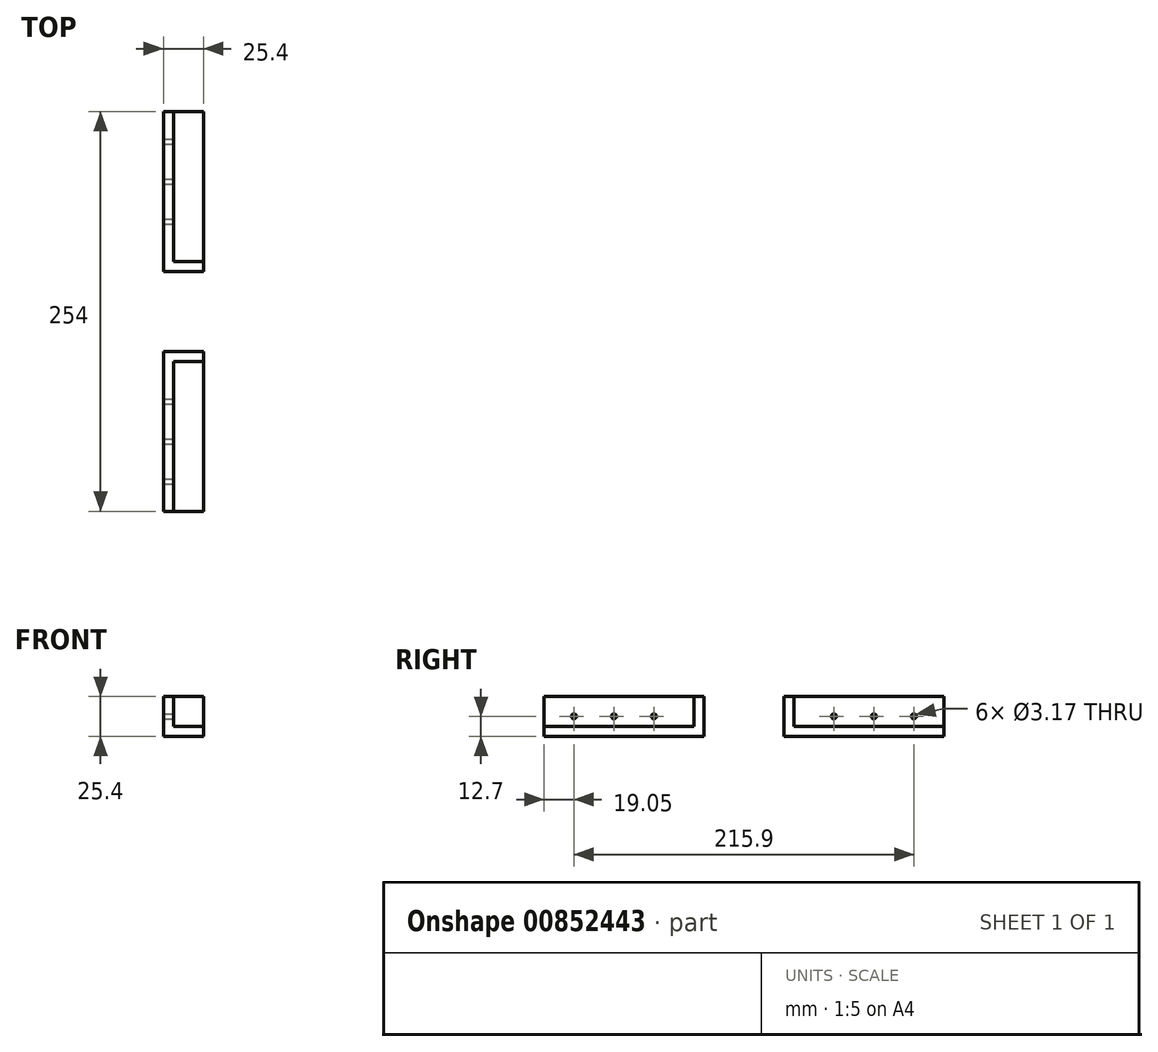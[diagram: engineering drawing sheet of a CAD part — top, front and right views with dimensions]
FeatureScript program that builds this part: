
annotation { "Feature Type Name" : "Feature", "Feature Type Description" : "" }
export const myFeature = defineFeature(function(context is Context, id is Id, definition is map)
    precondition{}
    {
        {
            var Q0;
            Q0=qCreatedBy(makeId("Front.planeOp"),FACE);
            var sketch = newSketch(context, id + "F0", { "sketchPlane" : qUnion([Q0])});
            skLineSegment(sketch, "E0", {"start": v(0, 0) * mm, "end": v(0, 25.4) * mm});
            skLineSegment(sketch, "E1", {"start": v(0, 25.4) * mm, "end": v(6.35, 25.4) * mm});
            skLineSegment(sketch, "E2", {"start": v(6.35, 25.4) * mm, "end": v(6.35, 6.35) * mm});
            skLineSegment(sketch, "E3", {"start": v(6.35, 6.35) * mm, "end": v(25.4, 6.35) * mm});
            skLineSegment(sketch, "E4", {"start": v(25.4, 6.35) * mm, "end": v(25.4, 0) * mm});
            skLineSegment(sketch, "E5", {"start": v(25.4, 0) * mm, "end": v(0, 0) * mm});
            skSolve(sketch);
        }
        {
            var Q0;
            Q0=qSketchRegion(id+"F0",true);
            extrude(context, id + "F1", {"entities" : qUnion([Q0]), "depth" : 101.6 * mm, "offsetDistance" : 25.4 * mm});
        }
        {
            var Q0;
            Q0=qCreatedBy(makeId("Front.planeOp"),FACE);
            var sketch = newSketch(context, id + "F2", { "sketchPlane" : qUnion([Q0])});
            skLineSegment(sketch, "E6.bottom", {"start": v(0, 0) * mm, "end": v(25.4, 0) * mm});
            skLineSegment(sketch, "E6.top", {"start": v(0, 25.4) * mm, "end": v(25.4, 25.4) * mm});
            skLineSegment(sketch, "E6.left", {"start": v(0, 0) * mm, "end": v(0, 25.4) * mm});
            skLineSegment(sketch, "E6.right", {"start": v(25.4, 0) * mm, "end": v(25.4, 25.4) * mm});
            skSolve(sketch);
        }
        {
            var Q0;
            Q0=qSketchRegion(id+"F2",true);
            extrude(context, id + "F3", {"entities" : qUnion([Q0]), "operationType" : NewBodyOperationType.ADD, "depth" : 6.35 * mm, "offsetDistance" : 25.4 * mm});
        }
        {
            var Q0;
            Q0=makeQuery(id+"F1.opExtrude","SWEPT_FACE",FACE,{"disambiguationData":[OSD([sQuery(id+"F0.wireOp",EDGE,"E2")])]});
            var sketch = newSketch(context, id + "F4", { "sketchPlane" : qUnion([Q0])});
            skLineSegment(sketch, "E7", {"start": v(-6.35, 12.7) * mm, "end": v(-101.6, 12.7) * mm, "construction": true});
            skCircle(sketch, "E8", {"center": v(-31.75, 12.7) * mm, "radius": 1.59 * mm});
            skCircle(sketch, "E9", {"center": v(-57.15, 12.7) * mm, "radius": 1.59 * mm});
            skCircle(sketch, "E10", {"center": v(-82.55, 12.7) * mm, "radius": 1.59 * mm});
            skSolve(sketch);
        }
        {
            var Q0;
            Q0=qSketchRegion(id+"F4",true);
            extrude(context, id + "F5", {"entities" : qUnion([Q0]), "operationType" : NewBodyOperationType.REMOVE, "oppositeDirection" : true, "depth" : 25.4 * mm, "offsetDistance" : 25.4 * mm});
        }
        {
            var Q0;
            Q0=qCreatedBy(makeId("Front.planeOp"),FACE);
            cPlane(context, id + "F6", {"entities" : qUnion([Q0]), "cplaneType" : CPlaneType.OFFSET, "offset" : 25.4 * mm, "oppositeDirection" : true, "width" : 152.4 * mm, "height" : 152.4 * mm});
        }
        {
            var Q0;
            Q0=makeQuery(id+"F1.opExtrude","SWEPT_BODY",BODY,{"disambiguationData":[OSD([sQuery(id+"F0.wireOp",EDGE,"E0"),sQuery(id+"F0.wireOp",EDGE,"E1"),sQuery(id+"F0.wireOp",EDGE,"E2"),sQuery(id+"F0.wireOp",EDGE,"E3"),sQuery(id+"F0.wireOp",EDGE,"E4"),sQuery(id+"F0.wireOp",EDGE,"E5")])]});
            var Q1;
            Q1=qCreatedBy(id+"F6.planeOp",FACE);
            mirror(context, id + "F7", {"entities" : qUnion([Q0]), "mirrorPlane" : qUnion([Q1])});
        }
    });
